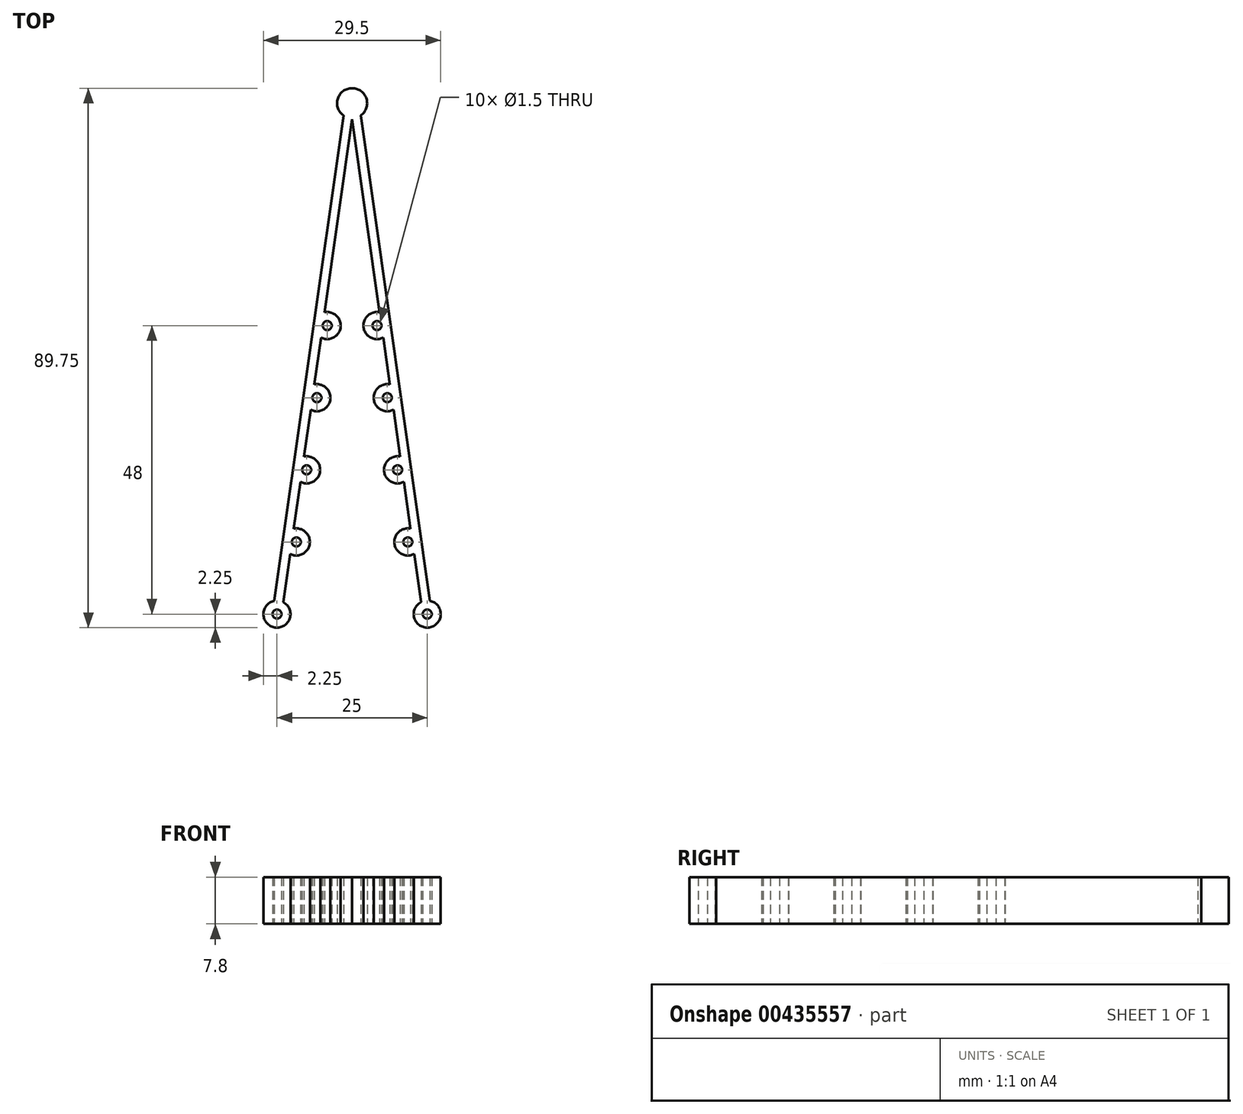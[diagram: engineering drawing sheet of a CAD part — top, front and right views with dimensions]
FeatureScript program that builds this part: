
annotation { "Feature Type Name" : "Feature", "Feature Type Description" : "" }
export const myFeature = defineFeature(function(context is Context, id is Id, definition is map)
    precondition{}
    {
        {
            var Q0;
            Q0=qCreatedBy(makeId("Top.planeOp"),FACE);
            var sketch = newSketch(context, id + "F0", { "sketchPlane" : qUnion([Q0])});
            skLineSegment(sketch, "E0", {"start": v(0, 0) * mm, "end": v(12.5, 0) * mm, "construction": true});
            skLineSegment(sketch, "E1", {"start": v(0, 85) * mm, "end": v(0, 0) * mm, "construction": true});
            skArc(sketch, "E2", {"start": v(1.43, 82.95) * mm, "mid": v(0, 87.5) * mm, "end": v(-1.43, 82.95) * mm});
            skCircle(sketch, "E3", {"center": v(-12.5, 0) * mm, "radius": 0.75 * mm});
            skCircle(sketch, "E4", {"center": v(12.5, 0) * mm, "radius": 0.75 * mm});
            skArc(sketch, "E5.0", {"start": v(-12.94, 2.2) * mm, "mid": v(-12.82, -2.23) * mm, "end": v(-11.46, 2) * mm});
            skArc(sketch, "E6.0", {"start": v(11.46, 2) * mm, "mid": v(12.82, -2.23) * mm, "end": v(12.94, 2.2) * mm});
            skCircle(sketch, "E7", {"center": v(0, 85) * mm, "radius": 1.13 * mm, "construction": true});
            skLineSegment(sketch, "E8", {"start": v(13.24, 0.1) * mm, "end": v(1.11, 85.16) * mm, "construction": true});
            skLineSegment(sketch, "E9", {"start": v(-13.24, 0.1) * mm, "end": v(-1.11, 85.16) * mm, "construction": true});
            skLineSegment(sketch, "E10.0", {"start": v(-11.76, -0.1) * mm, "end": v(0.22, 83.9) * mm, "construction": true});
            skLineSegment(sketch, "E11", {"start": v(-1.43, 82.95) * mm, "end": v(-12.94, 2.2) * mm});
            skLineSegment(sketch, "E12", {"start": v(-11.46, 2) * mm, "end": v(-10.32, 10) * mm});
            skLineSegment(sketch, "E13", {"start": v(12.94, 2.2) * mm, "end": v(1.43, 82.95) * mm});
            skLineSegment(sketch, "E14.0", {"start": v(-10.03, 12) * mm, "end": v(10.03, 12) * mm, "construction": true});
            skLineSegment(sketch, "E15.0", {"start": v(-8.32, 24) * mm, "end": v(8.32, 24) * mm, "construction": true});
            skLineSegment(sketch, "E16.0", {"start": v(-6.6, 36) * mm, "end": v(6.6, 36) * mm, "construction": true});
            skLineSegment(sketch, "E17.0", {"start": v(-4.9, 48) * mm, "end": v(4.9, 48) * mm, "construction": true});
            skCircle(sketch, "E18", {"center": v(-9.27, 12) * mm, "radius": 0.75 * mm});
            skCircle(sketch, "E19", {"center": v(-7.56, 24) * mm, "radius": 0.75 * mm});
            skCircle(sketch, "E20", {"center": v(-5.85, 36) * mm, "radius": 0.75 * mm});
            skCircle(sketch, "E21", {"center": v(-4.14, 48) * mm, "radius": 0.75 * mm});
            skCircle(sketch, "E22", {"center": v(4.14, 48) * mm, "radius": 0.75 * mm});
            skCircle(sketch, "E23", {"center": v(5.85, 36) * mm, "radius": 0.75 * mm});
            skCircle(sketch, "E24", {"center": v(7.56, 24) * mm, "radius": 0.75 * mm});
            skCircle(sketch, "E25", {"center": v(9.27, 12) * mm, "radius": 0.75 * mm});
            skArc(sketch, "E26.0", {"start": v(-10.32, 10) * mm, "mid": v(-7.05, 11.68) * mm, "end": v(-9.72, 14.2) * mm});
            skArc(sketch, "E27.0", {"start": v(-8.6, 22) * mm, "mid": v(-5.33, 23.68) * mm, "end": v(-8, 26.2) * mm});
            skArc(sketch, "E28.0", {"start": v(-6.9, 34) * mm, "mid": v(-3.62, 35.68) * mm, "end": v(-6.3, 38.2) * mm});
            skArc(sketch, "E29.0", {"start": v(-5.18, 46) * mm, "mid": v(-1.91, 47.68) * mm, "end": v(-4.58, 50.2) * mm});
            skLineSegment(sketch, "E30.trimOffspring", {"start": v(-9.72, 14.2) * mm, "end": v(-8.6, 22) * mm});
            skLineSegment(sketch, "E31.trimOffspring", {"start": v(-4.58, 50.2) * mm, "end": v(0, 82.34) * mm});
            skLineSegment(sketch, "E32.trimOffspring", {"start": v(-6.3, 38.2) * mm, "end": v(-5.18, 46) * mm});
            skLineSegment(sketch, "E33.trimOffspring", {"start": v(-8, 26.2) * mm, "end": v(-6.9, 34) * mm});
            skLineSegment(sketch, "E34.0", {"start": v(11.76, -0.1) * mm, "end": v(-0.22, 83.9) * mm, "construction": true});
            skArc(sketch, "E35.0", {"start": v(4.58, 50.2) * mm, "mid": v(1.91, 47.68) * mm, "end": v(5.18, 46) * mm});
            skArc(sketch, "E36.0", {"start": v(6.3, 38.2) * mm, "mid": v(3.62, 35.68) * mm, "end": v(6.9, 34) * mm});
            skArc(sketch, "E37.0", {"start": v(8, 26.2) * mm, "mid": v(5.33, 23.68) * mm, "end": v(8.6, 22) * mm});
            skArc(sketch, "E38.0", {"start": v(9.72, 14.2) * mm, "mid": v(7.05, 11.68) * mm, "end": v(10.32, 10) * mm});
            skLineSegment(sketch, "E39", {"start": v(11.46, 2) * mm, "end": v(10.32, 10) * mm});
            skLineSegment(sketch, "E40", {"start": v(9.72, 14.2) * mm, "end": v(8.6, 22) * mm});
            skLineSegment(sketch, "E41", {"start": v(8, 26.2) * mm, "end": v(6.9, 34) * mm});
            skLineSegment(sketch, "E42", {"start": v(6.3, 38.2) * mm, "end": v(5.18, 46) * mm});
            skLineSegment(sketch, "E43", {"start": v(4.58, 50.2) * mm, "end": v(0, 82.34) * mm});
            skSolve(sketch);
        }
        {
            var Q0;
            Q0=makeQuery(id+"F0.imprint","IMPRINT",FACE,{"disambiguationData":[TD([[makeQuery(id+"F0.imprint","IMPRINT",EDGE,{"derivedFrom":sQuery(id+"F0.wireOp",EDGE,"E2")}),1.0]])]});
            extrude(context, id + "F1", {"entities" : qUnion([Q0]), "endBound" : BoundingType.SYMMETRIC, "depth" : 7.8 * mm});
        }
    });
